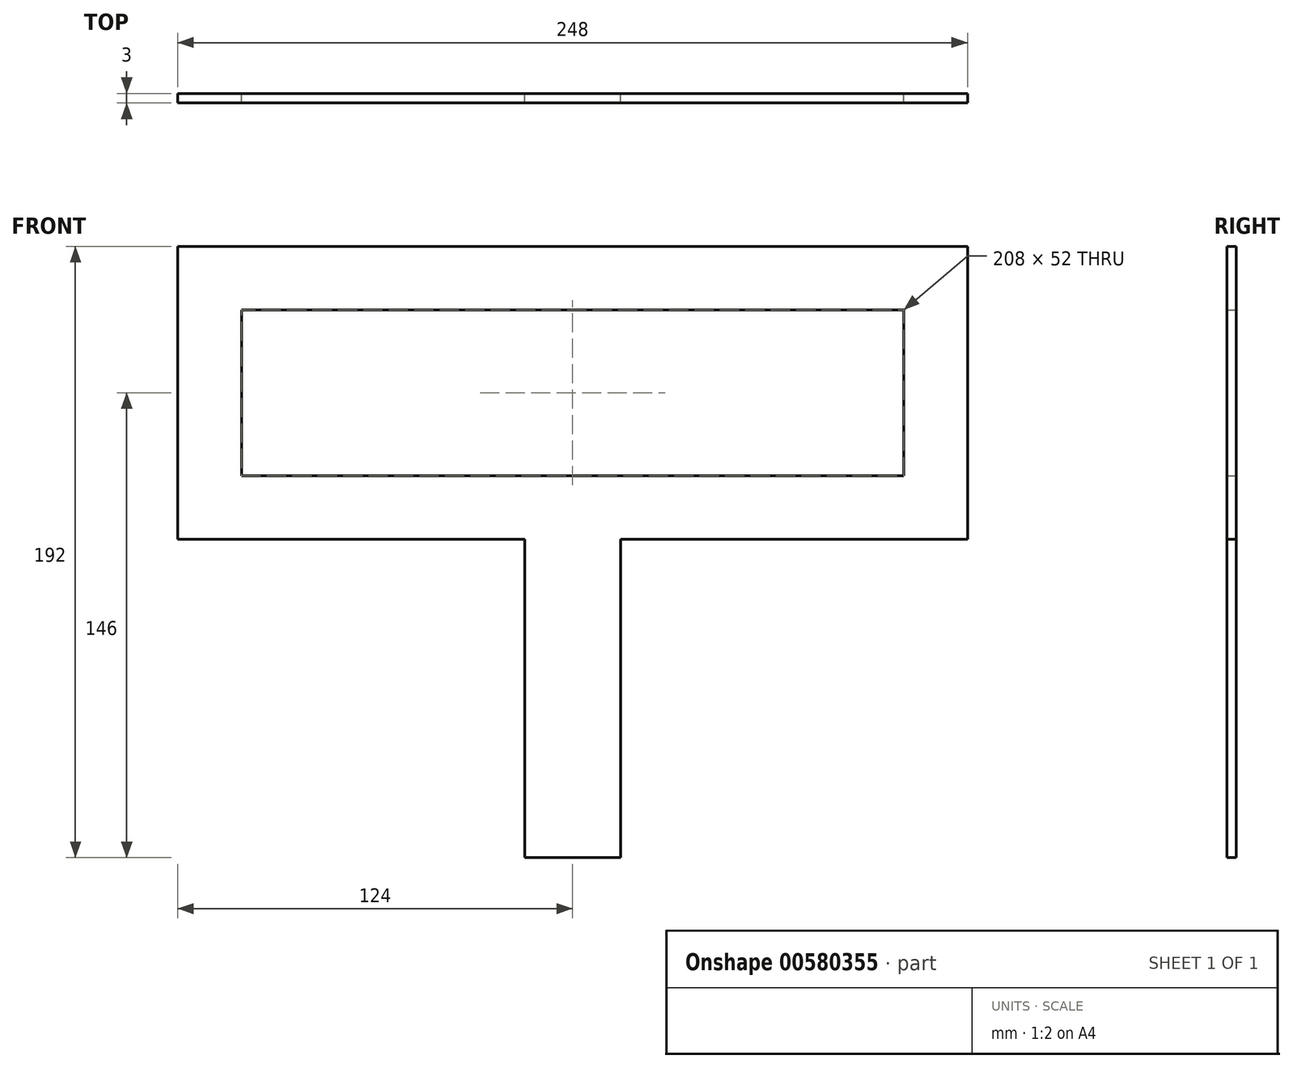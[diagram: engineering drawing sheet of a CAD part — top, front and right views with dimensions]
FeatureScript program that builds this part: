
annotation { "Feature Type Name" : "Feature", "Feature Type Description" : "" }
export const myFeature = defineFeature(function(context is Context, id is Id, definition is map)
    precondition{}
    {
        {
            var Q0;
            Q0=qCreatedBy(makeId("Front.planeOp"),FACE);
            var sketch = newSketch(context, id + "F0", { "sketchPlane" : qUnion([Q0])});
            skLineSegment(sketch, "E0.bottom", {"start": v(124, -46) * mm, "end": v(15, -46) * mm});
            skLineSegment(sketch, "E0.top", {"start": v(124, 46) * mm, "end": v(-124, 46) * mm});
            skLineSegment(sketch, "E0.left", {"start": v(124, -46) * mm, "end": v(124, 46) * mm});
            skLineSegment(sketch, "E0.right", {"start": v(-124, -46) * mm, "end": v(-124, 46) * mm});
            skPoint(sketch, "E0.middle", {"position": v(0, 0) * mm});
            skLineSegment(sketch, "E1.bottom", {"start": v(15, -146) * mm, "end": v(-15, -146) * mm});
            skLineSegment(sketch, "E1.left", {"start": v(15, -146) * mm, "end": v(15, -46) * mm});
            skLineSegment(sketch, "E1.right", {"start": v(-15, -146) * mm, "end": v(-15, -46) * mm});
            skPoint(sketch, "E1.middle", {"position": v(0, -96) * mm});
            skLineSegment(sketch, "E2.0", {"start": v(104, 26) * mm, "end": v(-104, 26) * mm});
            skLineSegment(sketch, "E2.1", {"start": v(104, -26) * mm, "end": v(104, 26) * mm});
            skLineSegment(sketch, "E2.2", {"start": v(104, -26) * mm, "end": v(-104, -26) * mm});
            skLineSegment(sketch, "E2.3", {"start": v(-104, -26) * mm, "end": v(-104, 26) * mm});
            skLineSegment(sketch, "E3.trimOffspring", {"start": v(-15, -46) * mm, "end": v(-124, -46) * mm});
            skSolve(sketch);
        }
        {
            var Q0;
            Q0=makeQuery(id+"F0.imprint","IMPRINT",FACE,{"disambiguationData":[TD([[makeQuery(id+"F0.imprint","IMPRINT",EDGE,{"derivedFrom":sQuery(id+"F0.wireOp",EDGE,"E0.bottom")}),-1.0]])]});
            extrude(context, id + "F1", {"entities" : qUnion([Q0]), "depth" : 3 * mm, "offsetDistance" : 25 * mm});
        }
    });
